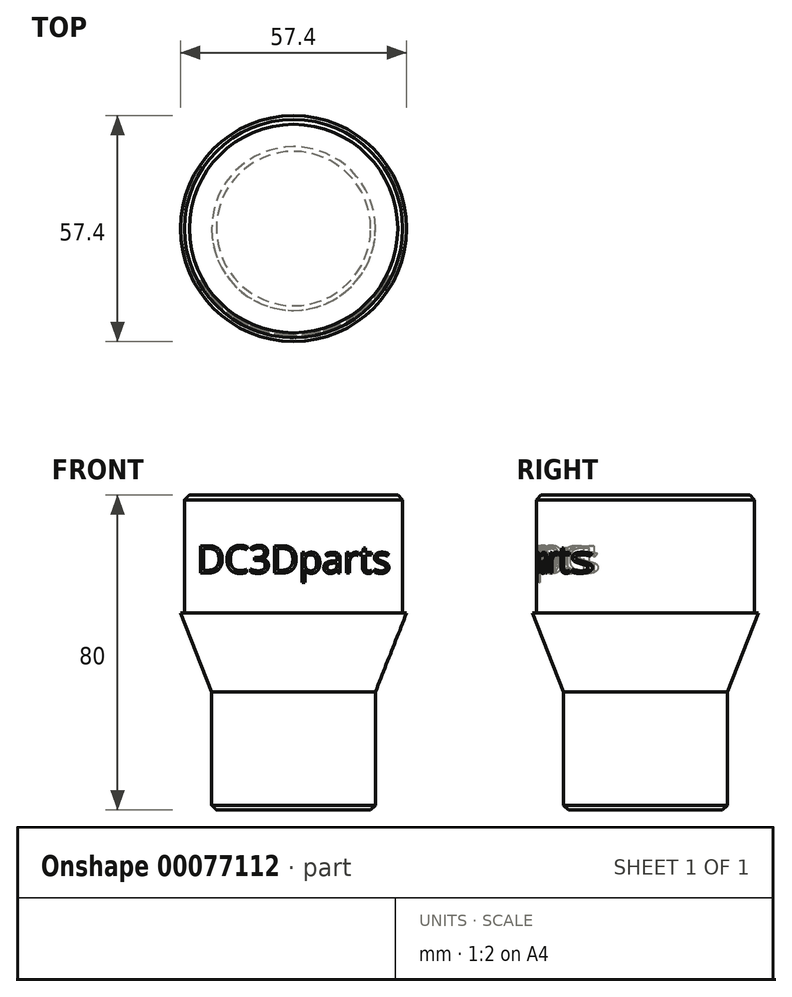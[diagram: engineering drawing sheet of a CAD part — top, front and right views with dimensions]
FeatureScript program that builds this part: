
annotation { "Feature Type Name" : "Feature", "Feature Type Description" : "" }
export const myFeature = defineFeature(function(context is Context, id is Id, definition is map)
    precondition{}
    {
        {
            var Q0;
            Q0=qCreatedBy(makeId("Front.planeOp"),FACE);
            var sketch = newSketch(context, id + "F0", { "sketchPlane" : qUnion([Q0])});
            skLineSegment(sketch, "E0", {"start": v(-27.68, 73.27) * mm, "end": v(-27.68, 43.27) * mm});
            skLineSegment(sketch, "E1", {"start": v(-27.68, 43.27) * mm, "end": v(-28.7, 43.27) * mm});
            skLineSegment(sketch, "E2", {"start": v(-28.7, 43.27) * mm, "end": v(-20.8, 23.27) * mm});
            skLineSegment(sketch, "E3", {"start": v(-20.8, 23.27) * mm, "end": v(-20.8, 23.27) * mm});
            skLineSegment(sketch, "E4", {"start": v(-20.8, 23.27) * mm, "end": v(-20.8, -6.73) * mm});
            skLineSegment(sketch, "E5", {"start": v(-20.8, -6.73) * mm, "end": v(0, -6.73) * mm});
            skLineSegment(sketch, "E6", {"start": v(-27.68, 73.27) * mm, "end": v(0, 73.27) * mm});
            skLineSegment(sketch, "E7", {"start": v(0, 94.78) * mm, "end": v(0, -99.97) * mm, "construction": true});
            skLineSegment(sketch, "E8", {"start": v(0, 73.27) * mm, "end": v(0, -6.73) * mm});
            skSolve(sketch);
        }
        {
            var Q0;
            Q0=makeQuery(id+"F0.imprint","IMPRINT",FACE,{"disambiguationData":[TD([[makeQuery(id+"F0.imprint","IMPRINT",EDGE,{"derivedFrom":sQuery(id+"F0.wireOp",EDGE,"E0")}),1.0]])]});
            var Q1;
            Q1=sQuery(id+"F0.wireOp",EDGE,"E7");
            revolve(context, id + "F1", {"entities" : qUnion([Q0]), "axis" : qUnion([Q1]), "revolveType" : RevolveType.FULL});
        }
        {
            var Q0;
            Q0=makeQuery(id+"F1.opRevolve","SWEPT_EDGE",EDGE,{"disambiguationData":[OSD([sQuery(id+"F0.wireOp",EDGE,"E0"),sQuery(id+"F0.wireOp",EDGE,"E6")])]});
            var Q1;
            Q1=makeQuery(id+"F1.opRevolve","SWEPT_EDGE",EDGE,{"disambiguationData":[OSD([sQuery(id+"F0.wireOp",EDGE,"E4"),sQuery(id+"F0.wireOp",EDGE,"E5")])]});
            chamfer(context, id + "F2", {"entities" : qUnion([Q0, Q1]), "width" : 1.2 * mm, "tangentPropagation" : true});
        }
        {
            var Q0;
            Q0=qCreatedBy(makeId("Front.planeOp"),FACE);
            cPlane(context, id + "F3", {"entities" : qUnion([Q0]), "cplaneType" : CPlaneType.OFFSET, "offset" : 40 * mm, "width" : 150 * mm, "height" : 150 * mm});
        }
        {
            var Q0;
            Q0=qCreatedBy(id+"F3.planeOp",FACE);
            var sketch = newSketch(context, id + "F4", { "sketchPlane" : qUnion([Q0])});
            skText(sketch, "E9", { "text": "DC3Dparts", "fontName": "OpenSans-Regular.ttf"});
            const initialGuessF4  = {"E9": [-0.0246, 0.05345, 1, 0, 0.007]};
            skSetInitialGuess(sketch, initialGuessF4);
            skSolve(sketch);
        }
        {
            var Q0;
            Q0 = qSketchRegion(id + "F4", true);
            var Q1;
            Q1=qCreatedBy(makeId("Front.planeOp"),FACE);
            extrude(context, id + "F5", {"entities" : qUnion([Q0]), "endBound" : BoundingType.UP_TO_SURFACE, "oppositeDirection" : true, "depth" : 25 * mm, "endBoundEntityFace" : qUnion([Q1]), "offsetDistance" : 25 * mm});
        }
        {
            var Q0;
            Q0=qCreatedBy(makeId("Front.planeOp"),FACE);
            var sketch = newSketch(context, id + "F6", { "sketchPlane" : qUnion([Q0])});
            skLineSegment(sketch, "E10.bottom", {"start": v(0, 46.95) * mm, "end": v(-27, 46.95) * mm});
            skLineSegment(sketch, "E10.top", {"start": v(0, 79.18) * mm, "end": v(-27, 79.18) * mm});
            skLineSegment(sketch, "E10.left", {"start": v(0, 46.95) * mm, "end": v(0, 79.18) * mm});
            skLineSegment(sketch, "E10.right", {"start": v(-27, 46.95) * mm, "end": v(-27, 79.18) * mm});
            skSolve(sketch);
        }
        {
            var Q0;
            Q0=makeQuery(id+"F6.imprint","IMPRINT",FACE,{"disambiguationData":[TD([[makeQuery(id+"F6.imprint","IMPRINT",EDGE,{"derivedFrom":sQuery(id+"F6.wireOp",EDGE,"E10.bottom")}),-1.0]])]});
            var Q1;
            Q1=sQuery(id+"F6.wireOp",EDGE,"E10.left");
            revolve(context, id + "F7", {"entities" : qUnion([Q0]), "axis" : qUnion([Q1]), "revolveType" : RevolveType.FULL});
        }
        {
            var Q0;
            Q0=makeQuery(id+"F7.opRevolve","SWEPT_BODY",BODY,{"disambiguationData":[OSD([sQuery(id+"F6.wireOp",EDGE,"E10.bottom"),sQuery(id+"F6.wireOp",EDGE,"E10.top"),sQuery(id+"F6.wireOp",EDGE,"E10.left"),sQuery(id+"F6.wireOp",EDGE,"E10.right")])]});
            var Q1;
            Q1=makeQuery(id+"F5.opExtrude","SWEPT_BODY",BODY,{"disambiguationData":[OSD([sQuery(id+"F4.wireOp",EDGE,"E9.sketch_text.stroke-0"),sQuery(id+"F4.wireOp",EDGE,"E9.sketch_text.stroke-1"),sQuery(id+"F4.wireOp",EDGE,"E9.sketch_text.stroke-2"),sQuery(id+"F4.wireOp",EDGE,"E9.sketch_text.stroke-3"),sQuery(id+"F4.wireOp",EDGE,"E9.sketch_text.stroke-4"),sQuery(id+"F4.wireOp",EDGE,"E9.sketch_text.stroke-5"),sQuery(id+"F4.wireOp",EDGE,"E9.sketch_text.stroke-6"),sQuery(id+"F4.wireOp",EDGE,"E9.sketch_text.stroke-7"),sQuery(id+"F4.wireOp",EDGE,"E9.sketch_text.stroke-8"),sQuery(id+"F4.wireOp",EDGE,"E9.sketch_text.stroke-9"),sQuery(id+"F4.wireOp",EDGE,"E9.sketch_text.stroke-10"),sQuery(id+"F4.wireOp",EDGE,"E9.sketch_text.stroke-11"),sQuery(id+"F4.wireOp",EDGE,"E9.sketch_text.stroke-12"),sQuery(id+"F4.wireOp",EDGE,"E9.sketch_text.stroke-13")])]});
            var Q2;
            Q2=makeQuery(id+"F5.opExtrude","SWEPT_BODY",BODY,{"disambiguationData":[OSD([sQuery(id+"F4.wireOp",EDGE,"E9.sketch_text.stroke-14"),sQuery(id+"F4.wireOp",EDGE,"E9.sketch_text.stroke-15"),sQuery(id+"F4.wireOp",EDGE,"E9.sketch_text.stroke-16"),sQuery(id+"F4.wireOp",EDGE,"E9.sketch_text.stroke-17"),sQuery(id+"F4.wireOp",EDGE,"E9.sketch_text.stroke-18"),sQuery(id+"F4.wireOp",EDGE,"E9.sketch_text.stroke-19"),sQuery(id+"F4.wireOp",EDGE,"E9.sketch_text.stroke-20"),sQuery(id+"F4.wireOp",EDGE,"E9.sketch_text.stroke-21"),sQuery(id+"F4.wireOp",EDGE,"E9.sketch_text.stroke-22"),sQuery(id+"F4.wireOp",EDGE,"E9.sketch_text.stroke-23"),sQuery(id+"F4.wireOp",EDGE,"E9.sketch_text.stroke-24"),sQuery(id+"F4.wireOp",EDGE,"E9.sketch_text.stroke-25"),sQuery(id+"F4.wireOp",EDGE,"E9.sketch_text.stroke-26"),sQuery(id+"F4.wireOp",EDGE,"E9.sketch_text.stroke-27"),sQuery(id+"F4.wireOp",EDGE,"E9.sketch_text.stroke-28")])]});
            var Q3;
            Q3=makeQuery(id+"F5.opExtrude","SWEPT_BODY",BODY,{"disambiguationData":[OSD([sQuery(id+"F4.wireOp",EDGE,"E9.sketch_text.stroke-29"),sQuery(id+"F4.wireOp",EDGE,"E9.sketch_text.stroke-30"),sQuery(id+"F4.wireOp",EDGE,"E9.sketch_text.stroke-31"),sQuery(id+"F4.wireOp",EDGE,"E9.sketch_text.stroke-32"),sQuery(id+"F4.wireOp",EDGE,"E9.sketch_text.stroke-33"),sQuery(id+"F4.wireOp",EDGE,"E9.sketch_text.stroke-34"),sQuery(id+"F4.wireOp",EDGE,"E9.sketch_text.stroke-35"),sQuery(id+"F4.wireOp",EDGE,"E9.sketch_text.stroke-36"),sQuery(id+"F4.wireOp",EDGE,"E9.sketch_text.stroke-37"),sQuery(id+"F4.wireOp",EDGE,"E9.sketch_text.stroke-38"),sQuery(id+"F4.wireOp",EDGE,"E9.sketch_text.stroke-39"),sQuery(id+"F4.wireOp",EDGE,"E9.sketch_text.stroke-40"),sQuery(id+"F4.wireOp",EDGE,"E9.sketch_text.stroke-41"),sQuery(id+"F4.wireOp",EDGE,"E9.sketch_text.stroke-42"),sQuery(id+"F4.wireOp",EDGE,"E9.sketch_text.stroke-43"),sQuery(id+"F4.wireOp",EDGE,"E9.sketch_text.stroke-44"),sQuery(id+"F4.wireOp",EDGE,"E9.sketch_text.stroke-45"),sQuery(id+"F4.wireOp",EDGE,"E9.sketch_text.stroke-46"),sQuery(id+"F4.wireOp",EDGE,"E9.sketch_text.stroke-47"),sQuery(id+"F4.wireOp",EDGE,"E9.sketch_text.stroke-48"),sQuery(id+"F4.wireOp",EDGE,"E9.sketch_text.stroke-49"),sQuery(id+"F4.wireOp",EDGE,"E9.sketch_text.stroke-50"),sQuery(id+"F4.wireOp",EDGE,"E9.sketch_text.stroke-51"),sQuery(id+"F4.wireOp",EDGE,"E9.sketch_text.stroke-52"),sQuery(id+"F4.wireOp",EDGE,"E9.sketch_text.stroke-53"),sQuery(id+"F4.wireOp",EDGE,"E9.sketch_text.stroke-54"),sQuery(id+"F4.wireOp",EDGE,"E9.sketch_text.stroke-55"),sQuery(id+"F4.wireOp",EDGE,"E9.sketch_text.stroke-56")])]});
            var Q4;
            Q4=makeQuery(id+"F5.opExtrude","SWEPT_BODY",BODY,{"disambiguationData":[OSD([sQuery(id+"F4.wireOp",EDGE,"E9.sketch_text.stroke-57"),sQuery(id+"F4.wireOp",EDGE,"E9.sketch_text.stroke-58"),sQuery(id+"F4.wireOp",EDGE,"E9.sketch_text.stroke-59"),sQuery(id+"F4.wireOp",EDGE,"E9.sketch_text.stroke-60"),sQuery(id+"F4.wireOp",EDGE,"E9.sketch_text.stroke-61"),sQuery(id+"F4.wireOp",EDGE,"E9.sketch_text.stroke-62"),sQuery(id+"F4.wireOp",EDGE,"E9.sketch_text.stroke-63"),sQuery(id+"F4.wireOp",EDGE,"E9.sketch_text.stroke-64"),sQuery(id+"F4.wireOp",EDGE,"E9.sketch_text.stroke-65"),sQuery(id+"F4.wireOp",EDGE,"E9.sketch_text.stroke-66"),sQuery(id+"F4.wireOp",EDGE,"E9.sketch_text.stroke-67"),sQuery(id+"F4.wireOp",EDGE,"E9.sketch_text.stroke-68"),sQuery(id+"F4.wireOp",EDGE,"E9.sketch_text.stroke-69"),sQuery(id+"F4.wireOp",EDGE,"E9.sketch_text.stroke-70")])]});
            var Q5;
            Q5=makeQuery(id+"F5.opExtrude","SWEPT_BODY",BODY,{"disambiguationData":[OSD([sQuery(id+"F4.wireOp",EDGE,"E9.sketch_text.stroke-71"),sQuery(id+"F4.wireOp",EDGE,"E9.sketch_text.stroke-72"),sQuery(id+"F4.wireOp",EDGE,"E9.sketch_text.stroke-73"),sQuery(id+"F4.wireOp",EDGE,"E9.sketch_text.stroke-74"),sQuery(id+"F4.wireOp",EDGE,"E9.sketch_text.stroke-75"),sQuery(id+"F4.wireOp",EDGE,"E9.sketch_text.stroke-76"),sQuery(id+"F4.wireOp",EDGE,"E9.sketch_text.stroke-77"),sQuery(id+"F4.wireOp",EDGE,"E9.sketch_text.stroke-78"),sQuery(id+"F4.wireOp",EDGE,"E9.sketch_text.stroke-79"),sQuery(id+"F4.wireOp",EDGE,"E9.sketch_text.stroke-80"),sQuery(id+"F4.wireOp",EDGE,"E9.sketch_text.stroke-81"),sQuery(id+"F4.wireOp",EDGE,"E9.sketch_text.stroke-82"),sQuery(id+"F4.wireOp",EDGE,"E9.sketch_text.stroke-83"),sQuery(id+"F4.wireOp",EDGE,"E9.sketch_text.stroke-84"),sQuery(id+"F4.wireOp",EDGE,"E9.sketch_text.stroke-85"),sQuery(id+"F4.wireOp",EDGE,"E9.sketch_text.stroke-86"),sQuery(id+"F4.wireOp",EDGE,"E9.sketch_text.stroke-87"),sQuery(id+"F4.wireOp",EDGE,"E9.sketch_text.stroke-88"),sQuery(id+"F4.wireOp",EDGE,"E9.sketch_text.stroke-89"),sQuery(id+"F4.wireOp",EDGE,"E9.sketch_text.stroke-90"),sQuery(id+"F4.wireOp",EDGE,"E9.sketch_text.stroke-91"),sQuery(id+"F4.wireOp",EDGE,"E9.sketch_text.stroke-92"),sQuery(id+"F4.wireOp",EDGE,"E9.sketch_text.stroke-93"),sQuery(id+"F4.wireOp",EDGE,"E9.sketch_text.stroke-94"),sQuery(id+"F4.wireOp",EDGE,"E9.sketch_text.stroke-95")])]});
            var Q6;
            Q6=makeQuery(id+"F5.opExtrude","SWEPT_BODY",BODY,{"disambiguationData":[OSD([sQuery(id+"F4.wireOp",EDGE,"E9.sketch_text.stroke-96"),sQuery(id+"F4.wireOp",EDGE,"E9.sketch_text.stroke-97"),sQuery(id+"F4.wireOp",EDGE,"E9.sketch_text.stroke-98"),sQuery(id+"F4.wireOp",EDGE,"E9.sketch_text.stroke-99"),sQuery(id+"F4.wireOp",EDGE,"E9.sketch_text.stroke-100"),sQuery(id+"F4.wireOp",EDGE,"E9.sketch_text.stroke-101"),sQuery(id+"F4.wireOp",EDGE,"E9.sketch_text.stroke-102"),sQuery(id+"F4.wireOp",EDGE,"E9.sketch_text.stroke-103"),sQuery(id+"F4.wireOp",EDGE,"E9.sketch_text.stroke-104"),sQuery(id+"F4.wireOp",EDGE,"E9.sketch_text.stroke-105"),sQuery(id+"F4.wireOp",EDGE,"E9.sketch_text.stroke-106"),sQuery(id+"F4.wireOp",EDGE,"E9.sketch_text.stroke-107"),sQuery(id+"F4.wireOp",EDGE,"E9.sketch_text.stroke-108"),sQuery(id+"F4.wireOp",EDGE,"E9.sketch_text.stroke-109"),sQuery(id+"F4.wireOp",EDGE,"E9.sketch_text.stroke-110"),sQuery(id+"F4.wireOp",EDGE,"E9.sketch_text.stroke-111"),sQuery(id+"F4.wireOp",EDGE,"E9.sketch_text.stroke-112"),sQuery(id+"F4.wireOp",EDGE,"E9.sketch_text.stroke-113"),sQuery(id+"F4.wireOp",EDGE,"E9.sketch_text.stroke-114"),sQuery(id+"F4.wireOp",EDGE,"E9.sketch_text.stroke-115"),sQuery(id+"F4.wireOp",EDGE,"E9.sketch_text.stroke-116"),sQuery(id+"F4.wireOp",EDGE,"E9.sketch_text.stroke-117"),sQuery(id+"F4.wireOp",EDGE,"E9.sketch_text.stroke-118"),sQuery(id+"F4.wireOp",EDGE,"E9.sketch_text.stroke-119"),sQuery(id+"F4.wireOp",EDGE,"E9.sketch_text.stroke-120"),sQuery(id+"F4.wireOp",EDGE,"E9.sketch_text.stroke-121"),sQuery(id+"F4.wireOp",EDGE,"E9.sketch_text.stroke-122")])]});
            var Q7;
            Q7=makeQuery(id+"F5.opExtrude","SWEPT_BODY",BODY,{"disambiguationData":[OSD([sQuery(id+"F4.wireOp",EDGE,"E9.sketch_text.stroke-123"),sQuery(id+"F4.wireOp",EDGE,"E9.sketch_text.stroke-124"),sQuery(id+"F4.wireOp",EDGE,"E9.sketch_text.stroke-125"),sQuery(id+"F4.wireOp",EDGE,"E9.sketch_text.stroke-126"),sQuery(id+"F4.wireOp",EDGE,"E9.sketch_text.stroke-127"),sQuery(id+"F4.wireOp",EDGE,"E9.sketch_text.stroke-128"),sQuery(id+"F4.wireOp",EDGE,"E9.sketch_text.stroke-129"),sQuery(id+"F4.wireOp",EDGE,"E9.sketch_text.stroke-130"),sQuery(id+"F4.wireOp",EDGE,"E9.sketch_text.stroke-131"),sQuery(id+"F4.wireOp",EDGE,"E9.sketch_text.stroke-132"),sQuery(id+"F4.wireOp",EDGE,"E9.sketch_text.stroke-133"),sQuery(id+"F4.wireOp",EDGE,"E9.sketch_text.stroke-134"),sQuery(id+"F4.wireOp",EDGE,"E9.sketch_text.stroke-135")])]});
            var Q8;
            Q8=makeQuery(id+"F5.opExtrude","SWEPT_BODY",BODY,{"disambiguationData":[OSD([sQuery(id+"F4.wireOp",EDGE,"E9.sketch_text.stroke-136"),sQuery(id+"F4.wireOp",EDGE,"E9.sketch_text.stroke-137"),sQuery(id+"F4.wireOp",EDGE,"E9.sketch_text.stroke-138"),sQuery(id+"F4.wireOp",EDGE,"E9.sketch_text.stroke-139"),sQuery(id+"F4.wireOp",EDGE,"E9.sketch_text.stroke-140"),sQuery(id+"F4.wireOp",EDGE,"E9.sketch_text.stroke-141"),sQuery(id+"F4.wireOp",EDGE,"E9.sketch_text.stroke-142"),sQuery(id+"F4.wireOp",EDGE,"E9.sketch_text.stroke-143"),sQuery(id+"F4.wireOp",EDGE,"E9.sketch_text.stroke-144"),sQuery(id+"F4.wireOp",EDGE,"E9.sketch_text.stroke-145"),sQuery(id+"F4.wireOp",EDGE,"E9.sketch_text.stroke-146"),sQuery(id+"F4.wireOp",EDGE,"E9.sketch_text.stroke-147"),sQuery(id+"F4.wireOp",EDGE,"E9.sketch_text.stroke-148"),sQuery(id+"F4.wireOp",EDGE,"E9.sketch_text.stroke-149"),sQuery(id+"F4.wireOp",EDGE,"E9.sketch_text.stroke-150"),sQuery(id+"F4.wireOp",EDGE,"E9.sketch_text.stroke-151"),sQuery(id+"F4.wireOp",EDGE,"E9.sketch_text.stroke-152"),sQuery(id+"F4.wireOp",EDGE,"E9.sketch_text.stroke-153"),sQuery(id+"F4.wireOp",EDGE,"E9.sketch_text.stroke-154")])]});
            var Q9;
            Q9=makeQuery(id+"F5.opExtrude","SWEPT_BODY",BODY,{"disambiguationData":[OSD([sQuery(id+"F4.wireOp",EDGE,"E9.sketch_text.stroke-155"),sQuery(id+"F4.wireOp",EDGE,"E9.sketch_text.stroke-156"),sQuery(id+"F4.wireOp",EDGE,"E9.sketch_text.stroke-157"),sQuery(id+"F4.wireOp",EDGE,"E9.sketch_text.stroke-158"),sQuery(id+"F4.wireOp",EDGE,"E9.sketch_text.stroke-159"),sQuery(id+"F4.wireOp",EDGE,"E9.sketch_text.stroke-160"),sQuery(id+"F4.wireOp",EDGE,"E9.sketch_text.stroke-161"),sQuery(id+"F4.wireOp",EDGE,"E9.sketch_text.stroke-162"),sQuery(id+"F4.wireOp",EDGE,"E9.sketch_text.stroke-163"),sQuery(id+"F4.wireOp",EDGE,"E9.sketch_text.stroke-164"),sQuery(id+"F4.wireOp",EDGE,"E9.sketch_text.stroke-165"),sQuery(id+"F4.wireOp",EDGE,"E9.sketch_text.stroke-166"),sQuery(id+"F4.wireOp",EDGE,"E9.sketch_text.stroke-167"),sQuery(id+"F4.wireOp",EDGE,"E9.sketch_text.stroke-168"),sQuery(id+"F4.wireOp",EDGE,"E9.sketch_text.stroke-169"),sQuery(id+"F4.wireOp",EDGE,"E9.sketch_text.stroke-170"),sQuery(id+"F4.wireOp",EDGE,"E9.sketch_text.stroke-171"),sQuery(id+"F4.wireOp",EDGE,"E9.sketch_text.stroke-172"),sQuery(id+"F4.wireOp",EDGE,"E9.sketch_text.stroke-173"),sQuery(id+"F4.wireOp",EDGE,"E9.sketch_text.stroke-174"),sQuery(id+"F4.wireOp",EDGE,"E9.sketch_text.stroke-175"),sQuery(id+"F4.wireOp",EDGE,"E9.sketch_text.stroke-176"),sQuery(id+"F4.wireOp",EDGE,"E9.sketch_text.stroke-177"),sQuery(id+"F4.wireOp",EDGE,"E9.sketch_text.stroke-178"),sQuery(id+"F4.wireOp",EDGE,"E9.sketch_text.stroke-179")])]});
            booleanBodies(context, id + "F8", {"operationType" : BooleanOperationType.SUBTRACTION, "tools" : qUnion([Q0]), "targets" : qUnion([Q1, Q2, Q3, Q4, Q5, Q6, Q7, Q8, Q9])});
        }
        {
            var Q0;
            Q0=makeQuery(id+"F5.opExtrude","SWEPT_BODY",BODY,{"disambiguationData":[OSD([sQuery(id+"F4.wireOp",EDGE,"E9.sketch_text.stroke-0"),sQuery(id+"F4.wireOp",EDGE,"E9.sketch_text.stroke-1"),sQuery(id+"F4.wireOp",EDGE,"E9.sketch_text.stroke-2"),sQuery(id+"F4.wireOp",EDGE,"E9.sketch_text.stroke-3"),sQuery(id+"F4.wireOp",EDGE,"E9.sketch_text.stroke-4"),sQuery(id+"F4.wireOp",EDGE,"E9.sketch_text.stroke-5"),sQuery(id+"F4.wireOp",EDGE,"E9.sketch_text.stroke-6"),sQuery(id+"F4.wireOp",EDGE,"E9.sketch_text.stroke-7"),sQuery(id+"F4.wireOp",EDGE,"E9.sketch_text.stroke-8"),sQuery(id+"F4.wireOp",EDGE,"E9.sketch_text.stroke-9"),sQuery(id+"F4.wireOp",EDGE,"E9.sketch_text.stroke-10"),sQuery(id+"F4.wireOp",EDGE,"E9.sketch_text.stroke-11"),sQuery(id+"F4.wireOp",EDGE,"E9.sketch_text.stroke-12"),sQuery(id+"F4.wireOp",EDGE,"E9.sketch_text.stroke-13")])]});
            var Q1;
            Q1=makeQuery(id+"F5.opExtrude","SWEPT_BODY",BODY,{"disambiguationData":[OSD([sQuery(id+"F4.wireOp",EDGE,"E9.sketch_text.stroke-14"),sQuery(id+"F4.wireOp",EDGE,"E9.sketch_text.stroke-15"),sQuery(id+"F4.wireOp",EDGE,"E9.sketch_text.stroke-16"),sQuery(id+"F4.wireOp",EDGE,"E9.sketch_text.stroke-17"),sQuery(id+"F4.wireOp",EDGE,"E9.sketch_text.stroke-18"),sQuery(id+"F4.wireOp",EDGE,"E9.sketch_text.stroke-19"),sQuery(id+"F4.wireOp",EDGE,"E9.sketch_text.stroke-20"),sQuery(id+"F4.wireOp",EDGE,"E9.sketch_text.stroke-21"),sQuery(id+"F4.wireOp",EDGE,"E9.sketch_text.stroke-22"),sQuery(id+"F4.wireOp",EDGE,"E9.sketch_text.stroke-23"),sQuery(id+"F4.wireOp",EDGE,"E9.sketch_text.stroke-24"),sQuery(id+"F4.wireOp",EDGE,"E9.sketch_text.stroke-25"),sQuery(id+"F4.wireOp",EDGE,"E9.sketch_text.stroke-26"),sQuery(id+"F4.wireOp",EDGE,"E9.sketch_text.stroke-27"),sQuery(id+"F4.wireOp",EDGE,"E9.sketch_text.stroke-28")])]});
            var Q2;
            Q2=makeQuery(id+"F5.opExtrude","SWEPT_BODY",BODY,{"disambiguationData":[OSD([sQuery(id+"F4.wireOp",EDGE,"E9.sketch_text.stroke-29"),sQuery(id+"F4.wireOp",EDGE,"E9.sketch_text.stroke-30"),sQuery(id+"F4.wireOp",EDGE,"E9.sketch_text.stroke-31"),sQuery(id+"F4.wireOp",EDGE,"E9.sketch_text.stroke-32"),sQuery(id+"F4.wireOp",EDGE,"E9.sketch_text.stroke-33"),sQuery(id+"F4.wireOp",EDGE,"E9.sketch_text.stroke-34"),sQuery(id+"F4.wireOp",EDGE,"E9.sketch_text.stroke-35"),sQuery(id+"F4.wireOp",EDGE,"E9.sketch_text.stroke-36"),sQuery(id+"F4.wireOp",EDGE,"E9.sketch_text.stroke-37"),sQuery(id+"F4.wireOp",EDGE,"E9.sketch_text.stroke-38"),sQuery(id+"F4.wireOp",EDGE,"E9.sketch_text.stroke-39"),sQuery(id+"F4.wireOp",EDGE,"E9.sketch_text.stroke-40"),sQuery(id+"F4.wireOp",EDGE,"E9.sketch_text.stroke-41"),sQuery(id+"F4.wireOp",EDGE,"E9.sketch_text.stroke-42"),sQuery(id+"F4.wireOp",EDGE,"E9.sketch_text.stroke-43"),sQuery(id+"F4.wireOp",EDGE,"E9.sketch_text.stroke-44"),sQuery(id+"F4.wireOp",EDGE,"E9.sketch_text.stroke-45"),sQuery(id+"F4.wireOp",EDGE,"E9.sketch_text.stroke-46"),sQuery(id+"F4.wireOp",EDGE,"E9.sketch_text.stroke-47"),sQuery(id+"F4.wireOp",EDGE,"E9.sketch_text.stroke-48"),sQuery(id+"F4.wireOp",EDGE,"E9.sketch_text.stroke-49"),sQuery(id+"F4.wireOp",EDGE,"E9.sketch_text.stroke-50"),sQuery(id+"F4.wireOp",EDGE,"E9.sketch_text.stroke-51"),sQuery(id+"F4.wireOp",EDGE,"E9.sketch_text.stroke-52"),sQuery(id+"F4.wireOp",EDGE,"E9.sketch_text.stroke-53"),sQuery(id+"F4.wireOp",EDGE,"E9.sketch_text.stroke-54"),sQuery(id+"F4.wireOp",EDGE,"E9.sketch_text.stroke-55"),sQuery(id+"F4.wireOp",EDGE,"E9.sketch_text.stroke-56")])]});
            var Q3;
            Q3=makeQuery(id+"F5.opExtrude","SWEPT_BODY",BODY,{"disambiguationData":[OSD([sQuery(id+"F4.wireOp",EDGE,"E9.sketch_text.stroke-57"),sQuery(id+"F4.wireOp",EDGE,"E9.sketch_text.stroke-58"),sQuery(id+"F4.wireOp",EDGE,"E9.sketch_text.stroke-59"),sQuery(id+"F4.wireOp",EDGE,"E9.sketch_text.stroke-60"),sQuery(id+"F4.wireOp",EDGE,"E9.sketch_text.stroke-61"),sQuery(id+"F4.wireOp",EDGE,"E9.sketch_text.stroke-62"),sQuery(id+"F4.wireOp",EDGE,"E9.sketch_text.stroke-63"),sQuery(id+"F4.wireOp",EDGE,"E9.sketch_text.stroke-64"),sQuery(id+"F4.wireOp",EDGE,"E9.sketch_text.stroke-65"),sQuery(id+"F4.wireOp",EDGE,"E9.sketch_text.stroke-66"),sQuery(id+"F4.wireOp",EDGE,"E9.sketch_text.stroke-67"),sQuery(id+"F4.wireOp",EDGE,"E9.sketch_text.stroke-68"),sQuery(id+"F4.wireOp",EDGE,"E9.sketch_text.stroke-69"),sQuery(id+"F4.wireOp",EDGE,"E9.sketch_text.stroke-70")])]});
            var Q4;
            Q4=makeQuery(id+"F5.opExtrude","SWEPT_BODY",BODY,{"disambiguationData":[OSD([sQuery(id+"F4.wireOp",EDGE,"E9.sketch_text.stroke-71"),sQuery(id+"F4.wireOp",EDGE,"E9.sketch_text.stroke-72"),sQuery(id+"F4.wireOp",EDGE,"E9.sketch_text.stroke-73"),sQuery(id+"F4.wireOp",EDGE,"E9.sketch_text.stroke-74"),sQuery(id+"F4.wireOp",EDGE,"E9.sketch_text.stroke-75"),sQuery(id+"F4.wireOp",EDGE,"E9.sketch_text.stroke-76"),sQuery(id+"F4.wireOp",EDGE,"E9.sketch_text.stroke-77"),sQuery(id+"F4.wireOp",EDGE,"E9.sketch_text.stroke-78"),sQuery(id+"F4.wireOp",EDGE,"E9.sketch_text.stroke-79"),sQuery(id+"F4.wireOp",EDGE,"E9.sketch_text.stroke-80"),sQuery(id+"F4.wireOp",EDGE,"E9.sketch_text.stroke-81"),sQuery(id+"F4.wireOp",EDGE,"E9.sketch_text.stroke-82"),sQuery(id+"F4.wireOp",EDGE,"E9.sketch_text.stroke-83"),sQuery(id+"F4.wireOp",EDGE,"E9.sketch_text.stroke-84"),sQuery(id+"F4.wireOp",EDGE,"E9.sketch_text.stroke-85"),sQuery(id+"F4.wireOp",EDGE,"E9.sketch_text.stroke-86"),sQuery(id+"F4.wireOp",EDGE,"E9.sketch_text.stroke-87"),sQuery(id+"F4.wireOp",EDGE,"E9.sketch_text.stroke-88"),sQuery(id+"F4.wireOp",EDGE,"E9.sketch_text.stroke-89"),sQuery(id+"F4.wireOp",EDGE,"E9.sketch_text.stroke-90"),sQuery(id+"F4.wireOp",EDGE,"E9.sketch_text.stroke-91"),sQuery(id+"F4.wireOp",EDGE,"E9.sketch_text.stroke-92"),sQuery(id+"F4.wireOp",EDGE,"E9.sketch_text.stroke-93"),sQuery(id+"F4.wireOp",EDGE,"E9.sketch_text.stroke-94"),sQuery(id+"F4.wireOp",EDGE,"E9.sketch_text.stroke-95")])]});
            var Q5;
            Q5=makeQuery(id+"F5.opExtrude","SWEPT_BODY",BODY,{"disambiguationData":[OSD([sQuery(id+"F4.wireOp",EDGE,"E9.sketch_text.stroke-96"),sQuery(id+"F4.wireOp",EDGE,"E9.sketch_text.stroke-97"),sQuery(id+"F4.wireOp",EDGE,"E9.sketch_text.stroke-98"),sQuery(id+"F4.wireOp",EDGE,"E9.sketch_text.stroke-99"),sQuery(id+"F4.wireOp",EDGE,"E9.sketch_text.stroke-100"),sQuery(id+"F4.wireOp",EDGE,"E9.sketch_text.stroke-101"),sQuery(id+"F4.wireOp",EDGE,"E9.sketch_text.stroke-102"),sQuery(id+"F4.wireOp",EDGE,"E9.sketch_text.stroke-103"),sQuery(id+"F4.wireOp",EDGE,"E9.sketch_text.stroke-104"),sQuery(id+"F4.wireOp",EDGE,"E9.sketch_text.stroke-105"),sQuery(id+"F4.wireOp",EDGE,"E9.sketch_text.stroke-106"),sQuery(id+"F4.wireOp",EDGE,"E9.sketch_text.stroke-107"),sQuery(id+"F4.wireOp",EDGE,"E9.sketch_text.stroke-108"),sQuery(id+"F4.wireOp",EDGE,"E9.sketch_text.stroke-109"),sQuery(id+"F4.wireOp",EDGE,"E9.sketch_text.stroke-110"),sQuery(id+"F4.wireOp",EDGE,"E9.sketch_text.stroke-111"),sQuery(id+"F4.wireOp",EDGE,"E9.sketch_text.stroke-112"),sQuery(id+"F4.wireOp",EDGE,"E9.sketch_text.stroke-113"),sQuery(id+"F4.wireOp",EDGE,"E9.sketch_text.stroke-114"),sQuery(id+"F4.wireOp",EDGE,"E9.sketch_text.stroke-115"),sQuery(id+"F4.wireOp",EDGE,"E9.sketch_text.stroke-116"),sQuery(id+"F4.wireOp",EDGE,"E9.sketch_text.stroke-117"),sQuery(id+"F4.wireOp",EDGE,"E9.sketch_text.stroke-118"),sQuery(id+"F4.wireOp",EDGE,"E9.sketch_text.stroke-119"),sQuery(id+"F4.wireOp",EDGE,"E9.sketch_text.stroke-120"),sQuery(id+"F4.wireOp",EDGE,"E9.sketch_text.stroke-121"),sQuery(id+"F4.wireOp",EDGE,"E9.sketch_text.stroke-122")])]});
            var Q6;
            Q6=makeQuery(id+"F5.opExtrude","SWEPT_BODY",BODY,{"disambiguationData":[OSD([sQuery(id+"F4.wireOp",EDGE,"E9.sketch_text.stroke-123"),sQuery(id+"F4.wireOp",EDGE,"E9.sketch_text.stroke-124"),sQuery(id+"F4.wireOp",EDGE,"E9.sketch_text.stroke-125"),sQuery(id+"F4.wireOp",EDGE,"E9.sketch_text.stroke-126"),sQuery(id+"F4.wireOp",EDGE,"E9.sketch_text.stroke-127"),sQuery(id+"F4.wireOp",EDGE,"E9.sketch_text.stroke-128"),sQuery(id+"F4.wireOp",EDGE,"E9.sketch_text.stroke-129"),sQuery(id+"F4.wireOp",EDGE,"E9.sketch_text.stroke-130"),sQuery(id+"F4.wireOp",EDGE,"E9.sketch_text.stroke-131"),sQuery(id+"F4.wireOp",EDGE,"E9.sketch_text.stroke-132"),sQuery(id+"F4.wireOp",EDGE,"E9.sketch_text.stroke-133"),sQuery(id+"F4.wireOp",EDGE,"E9.sketch_text.stroke-134"),sQuery(id+"F4.wireOp",EDGE,"E9.sketch_text.stroke-135")])]});
            var Q7;
            Q7=makeQuery(id+"F5.opExtrude","SWEPT_BODY",BODY,{"disambiguationData":[OSD([sQuery(id+"F4.wireOp",EDGE,"E9.sketch_text.stroke-136"),sQuery(id+"F4.wireOp",EDGE,"E9.sketch_text.stroke-137"),sQuery(id+"F4.wireOp",EDGE,"E9.sketch_text.stroke-138"),sQuery(id+"F4.wireOp",EDGE,"E9.sketch_text.stroke-139"),sQuery(id+"F4.wireOp",EDGE,"E9.sketch_text.stroke-140"),sQuery(id+"F4.wireOp",EDGE,"E9.sketch_text.stroke-141"),sQuery(id+"F4.wireOp",EDGE,"E9.sketch_text.stroke-142"),sQuery(id+"F4.wireOp",EDGE,"E9.sketch_text.stroke-143"),sQuery(id+"F4.wireOp",EDGE,"E9.sketch_text.stroke-144"),sQuery(id+"F4.wireOp",EDGE,"E9.sketch_text.stroke-145"),sQuery(id+"F4.wireOp",EDGE,"E9.sketch_text.stroke-146"),sQuery(id+"F4.wireOp",EDGE,"E9.sketch_text.stroke-147"),sQuery(id+"F4.wireOp",EDGE,"E9.sketch_text.stroke-148"),sQuery(id+"F4.wireOp",EDGE,"E9.sketch_text.stroke-149"),sQuery(id+"F4.wireOp",EDGE,"E9.sketch_text.stroke-150"),sQuery(id+"F4.wireOp",EDGE,"E9.sketch_text.stroke-151"),sQuery(id+"F4.wireOp",EDGE,"E9.sketch_text.stroke-152"),sQuery(id+"F4.wireOp",EDGE,"E9.sketch_text.stroke-153"),sQuery(id+"F4.wireOp",EDGE,"E9.sketch_text.stroke-154")])]});
            var Q8;
            Q8=makeQuery(id+"F5.opExtrude","SWEPT_BODY",BODY,{"disambiguationData":[OSD([sQuery(id+"F4.wireOp",EDGE,"E9.sketch_text.stroke-155"),sQuery(id+"F4.wireOp",EDGE,"E9.sketch_text.stroke-156"),sQuery(id+"F4.wireOp",EDGE,"E9.sketch_text.stroke-157"),sQuery(id+"F4.wireOp",EDGE,"E9.sketch_text.stroke-158"),sQuery(id+"F4.wireOp",EDGE,"E9.sketch_text.stroke-159"),sQuery(id+"F4.wireOp",EDGE,"E9.sketch_text.stroke-160"),sQuery(id+"F4.wireOp",EDGE,"E9.sketch_text.stroke-161"),sQuery(id+"F4.wireOp",EDGE,"E9.sketch_text.stroke-162"),sQuery(id+"F4.wireOp",EDGE,"E9.sketch_text.stroke-163"),sQuery(id+"F4.wireOp",EDGE,"E9.sketch_text.stroke-164"),sQuery(id+"F4.wireOp",EDGE,"E9.sketch_text.stroke-165"),sQuery(id+"F4.wireOp",EDGE,"E9.sketch_text.stroke-166"),sQuery(id+"F4.wireOp",EDGE,"E9.sketch_text.stroke-167"),sQuery(id+"F4.wireOp",EDGE,"E9.sketch_text.stroke-168"),sQuery(id+"F4.wireOp",EDGE,"E9.sketch_text.stroke-169"),sQuery(id+"F4.wireOp",EDGE,"E9.sketch_text.stroke-170"),sQuery(id+"F4.wireOp",EDGE,"E9.sketch_text.stroke-171"),sQuery(id+"F4.wireOp",EDGE,"E9.sketch_text.stroke-172"),sQuery(id+"F4.wireOp",EDGE,"E9.sketch_text.stroke-173"),sQuery(id+"F4.wireOp",EDGE,"E9.sketch_text.stroke-174"),sQuery(id+"F4.wireOp",EDGE,"E9.sketch_text.stroke-175"),sQuery(id+"F4.wireOp",EDGE,"E9.sketch_text.stroke-176"),sQuery(id+"F4.wireOp",EDGE,"E9.sketch_text.stroke-177"),sQuery(id+"F4.wireOp",EDGE,"E9.sketch_text.stroke-178"),sQuery(id+"F4.wireOp",EDGE,"E9.sketch_text.stroke-179")])]});
            var Q9;
            Q9=makeQuery(id+"F1.opRevolve","SWEPT_BODY",BODY,{"disambiguationData":[OSD([sQuery(id+"F0.wireOp",EDGE,"E0"),sQuery(id+"F0.wireOp",EDGE,"E1"),sQuery(id+"F0.wireOp",EDGE,"E2"),sQuery(id+"F0.wireOp",EDGE,"E4"),sQuery(id+"F0.wireOp",EDGE,"E5"),sQuery(id+"F0.wireOp",EDGE,"E6"),sQuery(id+"F0.wireOp",EDGE,"E8")])]});
            booleanBodies(context, id + "F9", {"operationType" : BooleanOperationType.SUBTRACTION, "tools" : qUnion([Q0, Q1, Q2, Q3, Q4, Q5, Q6, Q7, Q8]), "targets" : qUnion([Q9])});
        }
    });
